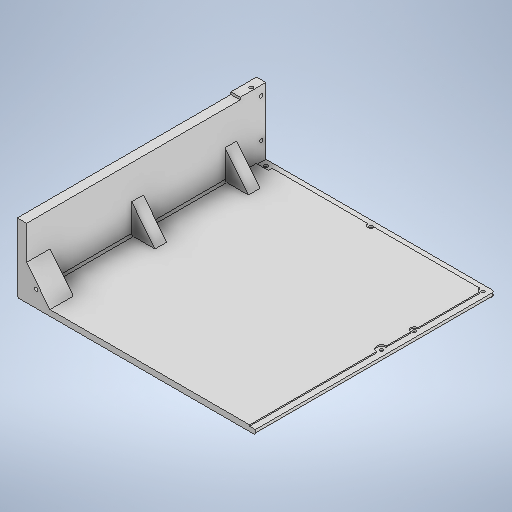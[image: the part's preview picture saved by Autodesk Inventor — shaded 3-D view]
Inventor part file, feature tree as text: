
AUTODESK INVENTOR PART (.ipt)
format: ipt  version: 2025.2 (Build 292293000, 293)  size: 790,528 bytes
history: native  units: mm
features: extrude x12, sketch x12, fillet x3, other x1
ambient origin geometry x8: Origin, YZ Plane, XZ Plane, XY Plane, X Axis, Y Axis, Z Axis, Center Point
bodies: Body1 (feature_tree)
feature tree (28):
  other  "ソリッド1"
  extrude  "押し出し1"  Depth=204.0mm
  extrude  "押し出し2"  Depth=205.0mm
  extrude  "押し出し3"  Depth=5.0mm TaperAngle=0.0deg
  extrude  "押し出し4"  Depth=8.0mm
  extrude  "押し出し5"  Depth=56.0mm TaperAngle=0.0deg
  extrude  "押し出し6"  Depth=22.0mm
  extrude  "押し出し7"  Depth=2.0mm TaperAngle=0.0deg
  extrude  "押し出し8"  Depth=3.0mm
  extrude  "押し出し9"  Depth=10.0mm
  extrude  "押し出し10"  Depth=5.5mm
  extrude  "押し出し11"  Depth=10.0mm TaperAngle=0.0deg
  extrude  "押し出し12"  Depth=3.0mm
  fillet  "フィレット1"  Radius=3.0mm
  fillet  "フィレット2"  Radius=8.0mm
  fillet  "フィレット3"  Radius=33.0mm
  sketch  "スケッチ1"
  sketch  "スケッチ2"
  sketch  "スケッチ3"
  sketch  "スケッチ4"
  sketch  "スケッチ5"
  sketch  "スケッチ6"
  sketch  "スケッチ7"
  sketch  "スケッチ8"
  sketch  "スケッチ9"
  sketch  "スケッチ10"
  sketch  "スケッチ11"
  sketch  "スケッチ12"
